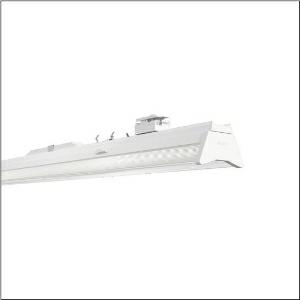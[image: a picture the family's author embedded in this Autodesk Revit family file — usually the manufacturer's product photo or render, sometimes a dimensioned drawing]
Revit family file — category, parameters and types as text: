
# Revit family: licross_11_performance_mo_51td16dn445g
name_source: partatom
category: Lighting Fixtures
units: mm (PartAtom-declared; Revit-internal decimal feet)

## family parameters
Cut with Voids When Loaded = No
Host = Face
Light Source = No
Part Type = Normal
Room Calculation Point = No
Round Connector Dimension = Use Diameter
Shared = No

## types (1)
- --- (1 x LED, 4520 lm, 24.3 W, 4000K)
    Apparent Load = 24 VA
    CIE Flux Codes = 66 88 96 79 100
    Color Rendering = 80
    Color Temperature = 4000K
    Default Elevation = 1800 mm
    Description = Licross 11 Performance MO, luminaire insert, of sheet steel, galvanised, coil coated, white, length: 1.500mm, width: 120mm, height: 123mm, LED rated luminous flux: 4.520lm, light colour: 840, SDCM (Standard Deviation of Colour Matching)MacAdam ≤ 2 SDCM (initial), control gear: DALI 2, with plug, 5-pole, with phase selection, mains connection: 220..240V, AC, 50/60Hz, rated input power: 24W, internal wiring halogen-free, primary light control with lens, of plastic, primary optical cover: cover, of PMMA, CAT 2 (L<= 3000cd/m²), light emission: direct/indirect distribution, primary light characteristic: symmetric, protection rating (complete): IP54, insulation class (complete): insulation class I (protective earthing), certification: CE, ENEC, VDE, UKCA, protection symbol: D if used in an environment with non-conductive dust loads with corresponding accessories, impact resistance: IK06, permissible ambient temperature for indoor applications: -25..+45°C, corresponds to IFS (International Featured Standards) requirements for safety and quality in the food industry, reducing of maximum allowable ambient temperature of 5°C with ceiling mounting, LABS conformity tested according to VDMA 24364:2018-05, The light source and the operating device comply with the requirements of the Ecodesign Regulation (EU) 2019/2020 and are replaceable in accordance with this regulation, packaging unit: 1 piece
    Height = 114 mm
    Lamp = 1 x LED
    Lamp Light Flux = 4520 lm
    Lamp Power = 24.3 W
    Lamp count = 1
    Length = 1500 mm
    Luminous efficacy = 186 lm/W
    Manufacturer = Siteco
    ModVariant = No
    Model = 51TD16DN445G
    Mounting Place = Ceiling
    Mounting Type = Pendant
    Number of Poles = 1
    OnlyDefault = Yes
    Power Factor = 1
    Product Name = Licross 11 Performance MO
    Product group = luminaire insert | ceiling pendant
    ProductGroupID = 901
    Protection Class = Protection class I
    Protection Degree = IP 54
    RLX_Detail_Level = 1
    RLX_Emergency_Light_Flux = 0 lm
    RLX_Emergency_Type = 0
    RLX_Emergency_Type_DB = No
    RlxData = <blob elided: 34065 chars, md5=39e6ce3f>
    Socket = socket
    Standby Power = 0 W
    System Light Flux = 4520 lm
    System Power = 24 W
    Type Comments = factory setting: luminous flux: 100 % | dim-lin: 254 | 161 mA
    Type Image = l_1256138.jpg
    URL = http://relux.com
    VarID = @adj_070871
    Voltage = 0 V
    Weight = 0.00 kg
    Width = 120 mm

## geometry (parser evidence)
native form markers: Blend x4, Sweep x13
no freeform markers — native parametric forms only
